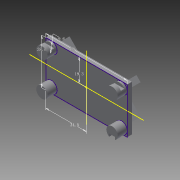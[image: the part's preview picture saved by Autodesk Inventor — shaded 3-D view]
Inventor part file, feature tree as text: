
AUTODESK INVENTOR PART (.ipt)
format: ipt  version: 2015 (Build 190159000, 159)  size: 195,584 bytes
history: native  units: mm
features: extrude x7, sketch x6, mirror x5, projected_geometry x3
ambient origin geometry x8: Origin, YZ Plane, XZ Plane, XY Plane, X Axis, Y Axis, Z Axis, Center Point
bodies: 实体1 (feature_tree)
feature tree (21):
  sketch  "草图1"  dims[d0=38.6mm d1=69.0mm]
  extrude  "拉伸1"  Depth=69.0mm
  extrude  "拉伸2"  Depth=34.5mm
  extrude  "拉伸3"  Depth=4.0mm TaperAngle=0.0deg
  mirror  "镜像1"
  extrude  "拉伸4"  Depth=1.8mm
  extrude  "拉伸5"  Depth=2.5mm
  extrude  "拉伸6"  Depth=2.5mm
  mirror  "镜像2"
  mirror  "镜像3"
  mirror  "镜像4"
  extrude  "拉伸7"  Depth=5.0mm
  mirror  "镜像5"
  sketch  "草图2"  dims[d2=34.5mm d3=19.3mm]
  projected_geometry  "投影回路1"
  sketch  "草图3"  dims[d4=9.6mm d5=4.0mm d6=0.0mm]
  projected_geometry  "投影回路2"
  sketch  "草图4"  dims[d7=8.0mm d8=0.0mm d9=1.8mm]
  sketch  "草图5"  dims[d10=3.0mm d11=2.5mm]
  projected_geometry  "投影回路3"
  sketch  "草图6"  dims[d12=8.0mm d13=0.0mm d17=2.5mm d18=5.0mm d19=3.0mm d20=8.0mm d21=0.0mm d22=5.0mm d23=12.0mm d24=10.0mm d25=0.0mm d26=3.0mm d27=5.0mm d28=10.0mm d29=0.0mm d30=3.0mm d31=2.5mm d32=1.8mm d33=10.0mm d34=0.0mm]
